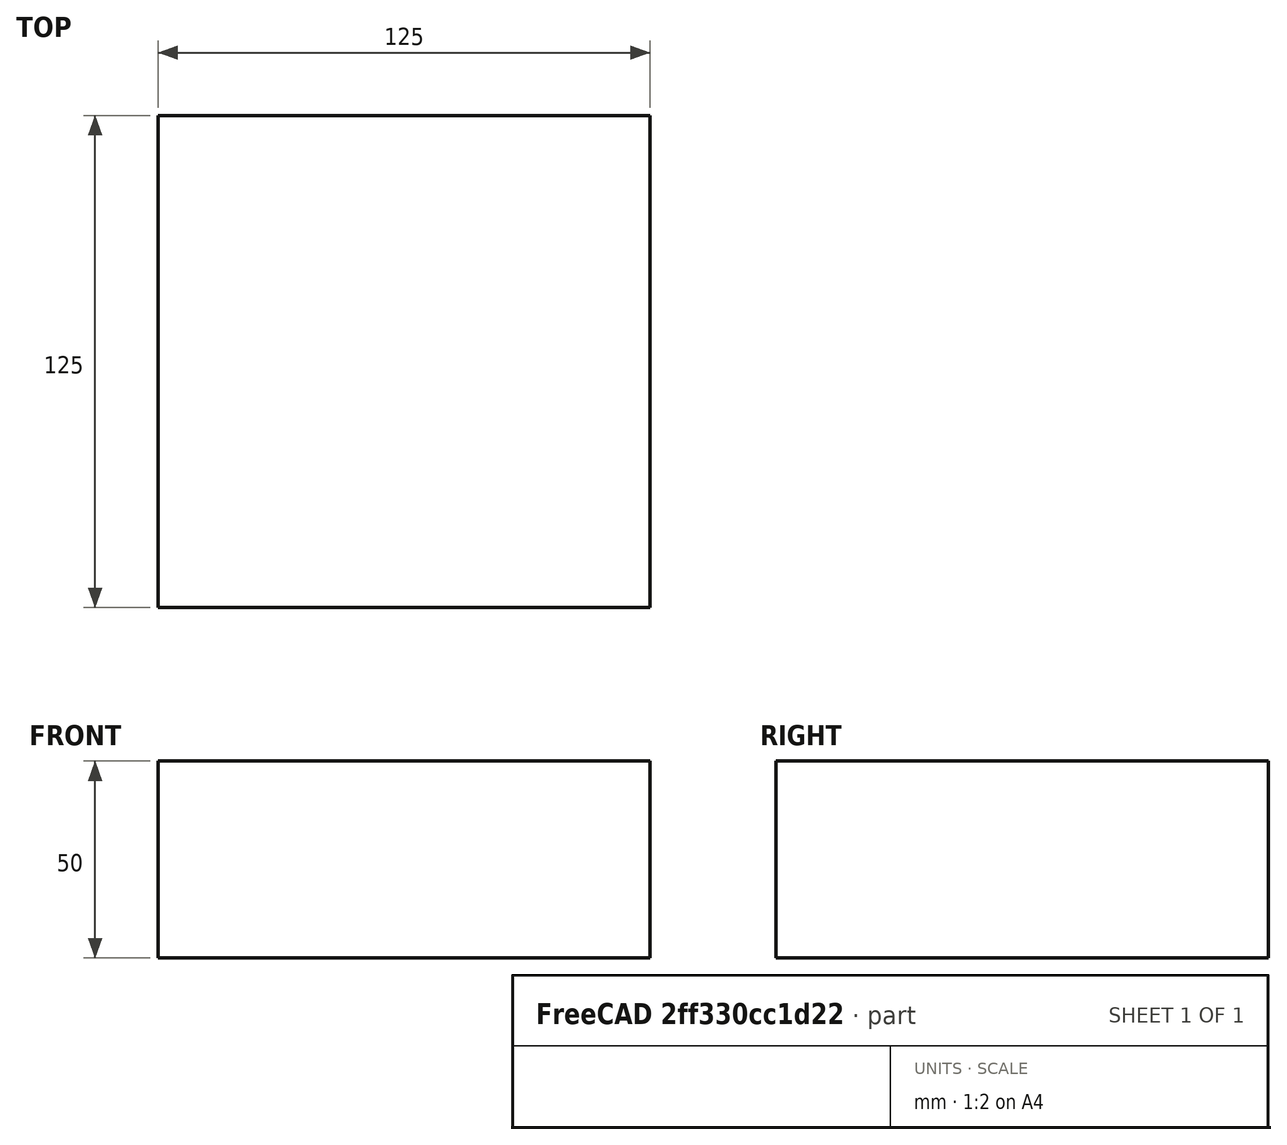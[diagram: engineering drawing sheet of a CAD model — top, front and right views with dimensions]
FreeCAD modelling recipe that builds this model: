
FCSTD DOCUMENT  (FreeCAD 0.15R4671 (Git))
Label: Square Bar 125 EN10059 S235JR
License: All rights reserved
LicenseURL: http://en.wikipedia.org/wiki/All_rights_reserved
objects: Sketcher::SketchObject×1, Part::Extrusion×1
note: 2 computed .brp shape members not serialized (recipe doc carries the construction recipe); baked Part::Feature solids carry a one-line shape summary decoded from their .brp

FEATURE [Sketcher::SketchObject] Sketch
  sketch-geometry (4):
    g0: LineSegment StartX=-62.5 StartY=-62.5 StartZ=0 EndX=62.5 EndY=-62.5 EndZ=0
    g1: LineSegment StartX=62.5 StartY=-62.5 StartZ=0 EndX=62.5 EndY=62.5 EndZ=0
    g2: LineSegment StartX=62.5 StartY=62.5 StartZ=0 EndX=-62.5 EndY=62.5 EndZ=0
    g3: LineSegment StartX=-62.5 StartY=62.5 StartZ=0 EndX=-62.5 EndY=-62.5 EndZ=0
  constraints (12):
    c: Coincident(g0,g1)
    c: Coincident(g1,g2)
    c: Coincident(g2,g3)
    c: Coincident(g3,g0)
    c: Horizontal(g0)
    c: Horizontal(g2)
    c: Vertical(g1)
    c: Vertical(g3)
    c: Symmetric(g1,g0,g-1)
    c: Symmetric(g2,g1,g-2)
    c: Equal(g1,g2)
    c: DistanceY(g1) = 125
FEATURE [Part::Extrusion] Extrude  label="Square Bar 125 EN10059 S235JR"
  Base = -> Sketch
  Dir = (0,0,50)
  Solid = true
